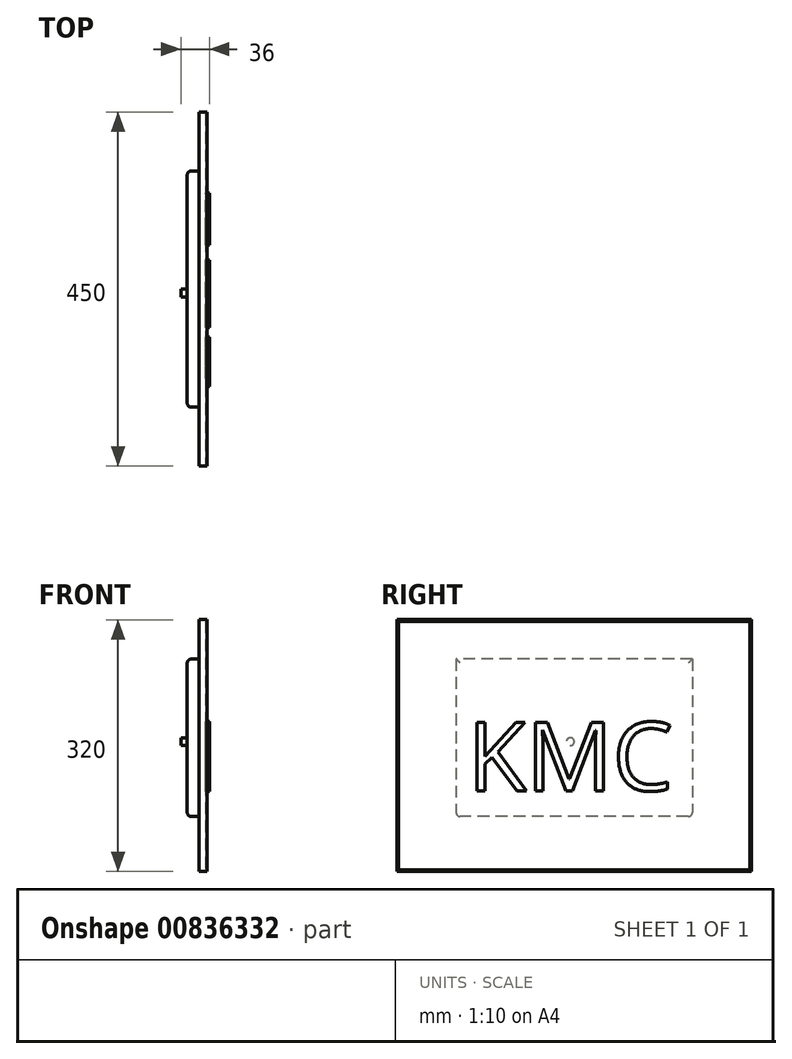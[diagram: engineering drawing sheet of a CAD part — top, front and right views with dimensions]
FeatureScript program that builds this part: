
annotation { "Feature Type Name" : "Feature", "Feature Type Description" : "" }
export const myFeature = defineFeature(function(context is Context, id is Id, definition is map)
    precondition{}
    {
        {
            var Q0;
            Q0=qCreatedBy(makeId("Right.planeOp"),FACE);
            var sketch = newSketch(context, id + "F0", { "sketchPlane" : qUnion([Q0])});
            skLineSegment(sketch, "E0.bottom", {"start": v(-46.28, 304.57) * mm, "end": v(403.72, 304.57) * mm});
            skLineSegment(sketch, "E0.top", {"start": v(-46.28, -15.43) * mm, "end": v(403.72, -15.43) * mm});
            skLineSegment(sketch, "E0.left", {"start": v(-46.28, 304.57) * mm, "end": v(-46.28, -15.43) * mm});
            skLineSegment(sketch, "E0.right", {"start": v(403.72, 304.57) * mm, "end": v(403.72, -15.43) * mm});
            skSolve(sketch);
        }
        {
            var Q0;
            Q0=makeQuery(id+"F0.imprint","IMPRINT",FACE,{"disambiguationData":[TD([[makeQuery(id+"F0.imprint","IMPRINT",EDGE,{"derivedFrom":sQuery(id+"F0.wireOp",EDGE,"E0.bottom")}),-1.0]])]});
            extrude(context, id + "F1", {"entities" : qUnion([Q0]), "depth" : 10 * mm, "offsetDistance" : 25 * mm});
        }
        {
            var Q0;
            Q0=makeQuery(id+"F1.opExtrude","CAP_FACE",FACE,{"disambiguationData":[OSD([sQuery(id+"F0.wireOp",EDGE,"E0.bottom"),sQuery(id+"F0.wireOp",EDGE,"E0.top"),sQuery(id+"F0.wireOp",EDGE,"E0.left"),sQuery(id+"F0.wireOp",EDGE,"E0.right")])],"isStart":false});
            var sketch = newSketch(context, id + "F2", { "sketchPlane" : qUnion([Q0])});
            skLineSegment(sketch, "E1.0", {"start": v(-44.28, 302.57) * mm, "end": v(-44.28, -13.43) * mm});
            skLineSegment(sketch, "E1.1", {"start": v(401.72, 302.57) * mm, "end": v(-44.28, 302.57) * mm});
            skLineSegment(sketch, "E1.2", {"start": v(401.72, -13.43) * mm, "end": v(401.72, 302.57) * mm});
            skLineSegment(sketch, "E1.3", {"start": v(-44.28, -13.43) * mm, "end": v(401.72, -13.43) * mm});
            skSolve(sketch);
        }
        {
            var Q0;
            Q0=makeQuery(id+"F2.imprint","IMPRINT",FACE,{"disambiguationData":[TD([[makeQuery(id+"F2.imprint","IMPRINT",EDGE,{"derivedFrom":sQuery(id+"F2.wireOp",EDGE,"E1.0")}),1.0]])]});
            extrude(context, id + "F3", {"entities" : qUnion([Q0]), "operationType" : NewBodyOperationType.REMOVE, "oppositeDirection" : true, "depth" : 2 * mm, "offsetDistance" : 25 * mm});
        }
        {
            var Q0;
            Q0=makeQuery(id+"F1.opExtrude","CAP_FACE",FACE,{"disambiguationData":[OSD([sQuery(id+"F0.wireOp",EDGE,"E0.bottom"),sQuery(id+"F0.wireOp",EDGE,"E0.top"),sQuery(id+"F0.wireOp",EDGE,"E0.left"),sQuery(id+"F0.wireOp",EDGE,"E0.right")])],"isStart":true});
            var sketch = newSketch(context, id + "F4", { "sketchPlane" : qUnion([Q0])});
            skLineSegment(sketch, "E2.bottom", {"start": v(-328.72, 254.57) * mm, "end": v(-28.72, 254.57) * mm});
            skLineSegment(sketch, "E2.top", {"start": v(-328.72, 54.57) * mm, "end": v(-28.72, 54.57) * mm});
            skLineSegment(sketch, "E2.left", {"start": v(-328.72, 254.57) * mm, "end": v(-328.72, 54.57) * mm});
            skLineSegment(sketch, "E2.right", {"start": v(-28.72, 254.57) * mm, "end": v(-28.72, 54.57) * mm});
            skSolve(sketch);
        }
        {
            var Q0;
            Q0=makeQuery(id+"F4.imprint","IMPRINT",FACE,{"disambiguationData":[TD([[makeQuery(id+"F4.imprint","IMPRINT",EDGE,{"derivedFrom":sQuery(id+"F4.wireOp",EDGE,"E2.bottom")}),-1.0]])]});
            extrude(context, id + "F5", {"entities" : qUnion([Q0]), "operationType" : NewBodyOperationType.ADD, "depth" : 15 * mm, "offsetDistance" : 25 * mm});
        }
        {
            var Q0;
            Q0=makeQuery(id+"F5.opExtrude","CAP_EDGE",EDGE,{"disambiguationData":[OSD([sQuery(id+"F4.wireOp",EDGE,"E2.bottom")])],"isStart":false});
            var Q1;
            Q1=makeQuery(id+"F5.opExtrude","CAP_EDGE",EDGE,{"disambiguationData":[OSD([sQuery(id+"F4.wireOp",EDGE,"E2.left")])],"isStart":false});
            var Q2;
            Q2=makeQuery(id+"F5.opExtrude","CAP_EDGE",EDGE,{"disambiguationData":[OSD([sQuery(id+"F4.wireOp",EDGE,"E2.bottom")])],"isStart":true});
            var Q3;
            Q3=makeQuery(id+"F5.opExtrude","CAP_EDGE",EDGE,{"disambiguationData":[OSD([sQuery(id+"F4.wireOp",EDGE,"E2.left")])],"isStart":true});
            var Q4;
            Q4=makeQuery(id+"F5.opExtrude","CAP_EDGE",EDGE,{"disambiguationData":[OSD([sQuery(id+"F4.wireOp",EDGE,"E2.top")])],"isStart":true});
            var Q5;
            Q5=makeQuery(id+"F5.opExtrude","CAP_EDGE",EDGE,{"disambiguationData":[OSD([sQuery(id+"F4.wireOp",EDGE,"E2.right")])],"isStart":true});
            var Q6;
            Q6=makeQuery(id+"F5.opExtrude","CAP_EDGE",EDGE,{"disambiguationData":[OSD([sQuery(id+"F4.wireOp",EDGE,"E2.right")])],"isStart":false});
            var Q7;
            Q7=makeQuery(id+"F5.opExtrude","SWEPT_EDGE",EDGE,{"disambiguationData":[OSD([sQuery(id+"F4.wireOp",EDGE,"E2.top"),sQuery(id+"F4.wireOp",EDGE,"E2.right")])]});
            var Q8;
            Q8=makeQuery(id+"F5.opExtrude","CAP_EDGE",EDGE,{"disambiguationData":[OSD([sQuery(id+"F4.wireOp",EDGE,"E2.top")])],"isStart":false});
            var Q9;
            Q9=makeQuery(id+"F5.opExtrude","SWEPT_EDGE",EDGE,{"disambiguationData":[OSD([sQuery(id+"F4.wireOp",EDGE,"E2.top"),sQuery(id+"F4.wireOp",EDGE,"E2.left")])]});
            fillet(context, id + "F6", {"entities" : qUnion([Q0, Q1, Q2, Q3, Q4, Q5, Q6, Q7, Q8, Q9]), "radius" : 5 * mm, "tangentPropagation" : true, "allowEdgeOverflow" : false});
        }
        {
            var Q0;
            Q0=makeQuery(id+"F5.opExtrude","CAP_FACE",FACE,{"disambiguationData":[OSD([sQuery(id+"F4.wireOp",EDGE,"E2.bottom"),sQuery(id+"F4.wireOp",EDGE,"E2.top"),sQuery(id+"F4.wireOp",EDGE,"E2.left"),sQuery(id+"F4.wireOp",EDGE,"E2.right")])],"isStart":false});
            var sketch = newSketch(context, id + "F7", { "sketchPlane" : qUnion([Q0])});
            skCircle(sketch, "E3", {"center": v(-173.72, 149.57) * mm, "radius": 5 * mm});
            skSolve(sketch);
        }
        {
            var Q0;
            Q0 = qSketchRegion(id + "F7", true);
            extrude(context, id + "F8", {"entities" : qUnion([Q0]), "operationType" : NewBodyOperationType.ADD, "depth" : 8 * mm, "offsetDistance" : 25 * mm});
        }
        {
            var Q0;
            Q0=makeQuery(id+"F3.boolean.opBoolean","COPY",FACE,{"derivedFrom":makeQuery(id+"F3.opExtrude","CAP_FACE",FACE,{"disambiguationData":[OSD([sQuery(id+"F2.wireOp",EDGE,"E1.0"),sQuery(id+"F2.wireOp",EDGE,"E1.1"),sQuery(id+"F2.wireOp",EDGE,"E1.2"),sQuery(id+"F2.wireOp",EDGE,"E1.3")])],"isStart":false})});
            var sketch = newSketch(context, id + "F9", { "sketchPlane" : qUnion([Q0])});
            skText(sketch, "E4", { "text": "KMC\n", "fontName": "OpenSans-Regular.ttf"});
            const initialGuessF9  = {"E4": [0.0431, 0.08736, 1, 0, 0.08751]};
            skSetInitialGuess(sketch, initialGuessF9);
            skSolve(sketch);
        }
        {
            var Q0;
            Q0 = qSketchRegion(id + "F9", true);
            extrude(context, id + "F10", {"entities" : qUnion([Q0]), "operationType" : NewBodyOperationType.ADD, "depth" : 5 * mm, "offsetDistance" : 25 * mm});
        }
    });
